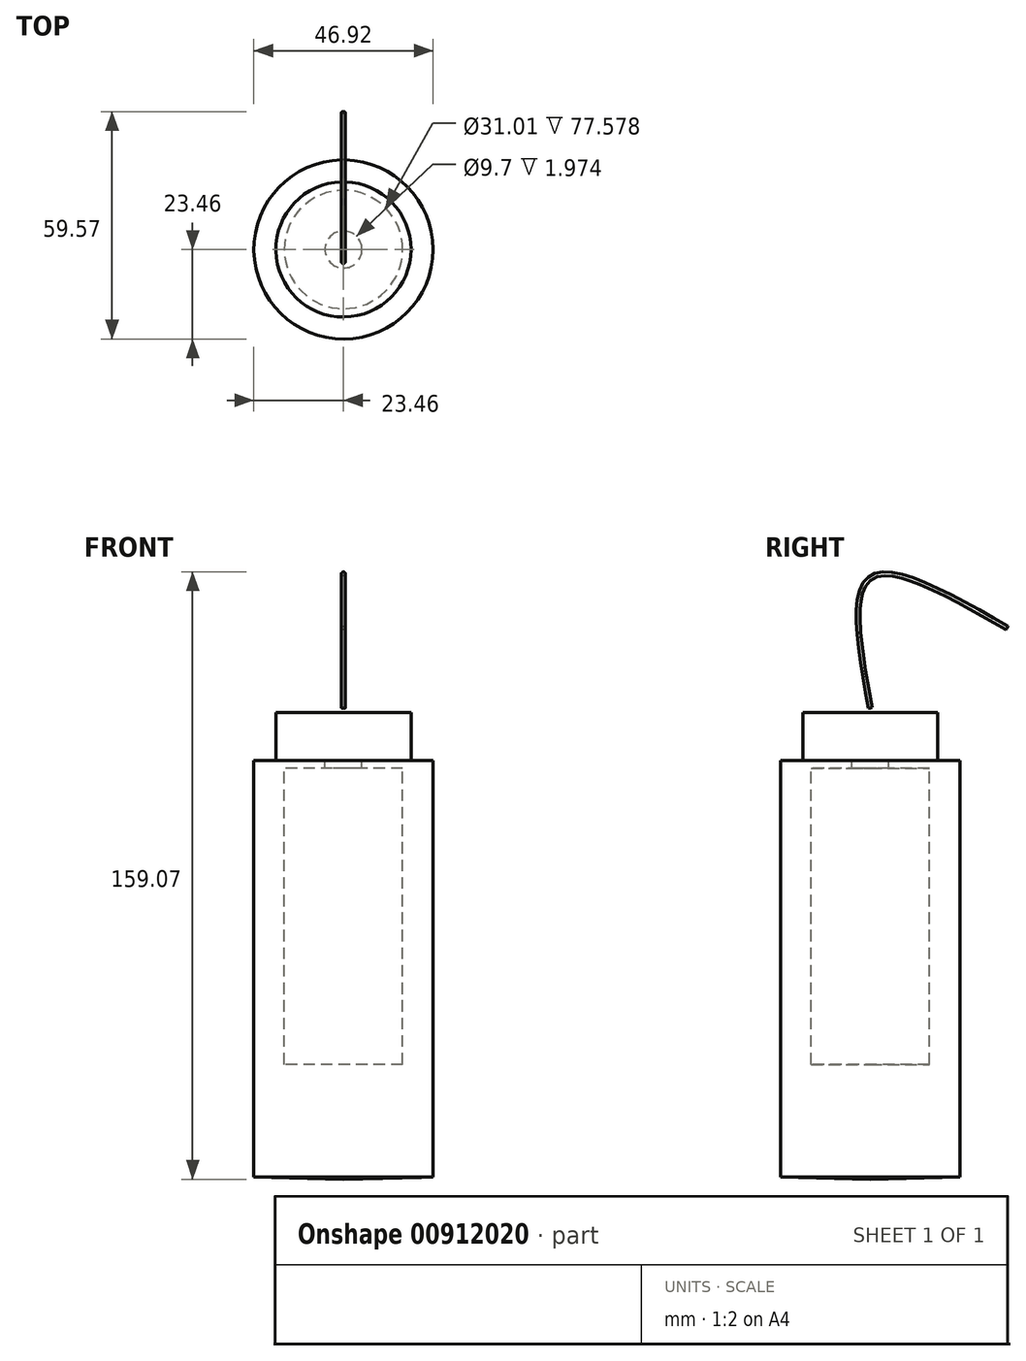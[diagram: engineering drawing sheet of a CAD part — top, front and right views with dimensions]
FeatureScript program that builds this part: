
annotation { "Feature Type Name" : "Feature", "Feature Type Description" : "" }
export const myFeature = defineFeature(function(context is Context, id is Id, definition is map)
    precondition{}
    {
        {
            var Q0;
            Q0=qCreatedBy(makeId("Front.planeOp"),FACE);
            var sketch = newSketch(context, id + "F0", { "sketchPlane" : qUnion([Q0])});
            skLineSegment(sketch, "E0", {"start": v(0, -24.73) * mm, "end": v(0, -54.83) * mm});
            skLineSegment(sketch, "E1", {"start": v(0, 54.83) * mm, "end": v(4.85, 54.83) * mm});
            skLineSegment(sketch, "E2", {"start": v(23.46, 54.83) * mm, "end": v(23.46, -54.25) * mm});
            skLineSegment(sketch, "E3", {"start": v(23.46, -54.25) * mm, "end": v(0, -54.83) * mm});
            skLineSegment(sketch, "E4", {"start": v(17.7, 54.83) * mm, "end": v(17.7, 67.48) * mm});
            skLineSegment(sketch, "E5", {"start": v(8.85, 67.48) * mm, "end": v(0, 67.48) * mm});
            skLineSegment(sketch, "E6", {"start": v(122.75, 33.82) * mm, "end": v(122.75, 27.49) * mm});
            skLineSegment(sketch, "E7", {"start": v(0, 67.48) * mm, "end": v(0, 54.83) * mm});
            skLineSegment(sketch, "E8", {"start": v(15.5, 52.85) * mm, "end": v(15.5, -24.73) * mm});
            skLineSegment(sketch, "E9", {"start": v(15.5, -24.73) * mm, "end": v(0, -24.73) * mm});
            skLineSegment(sketch, "E10", {"start": v(15.5, 52.85) * mm, "end": v(4.85, 52.85) * mm});
            skLineSegment(sketch, "E11", {"start": v(4.85, 52.85) * mm, "end": v(4.85, 54.83) * mm});
            skLineSegment(sketch, "E12.trimOffspring", {"start": v(17.7, 54.83) * mm, "end": v(23.46, 54.83) * mm});
            skLineSegment(sketch, "E13", {"start": v(8.85, 67.48) * mm, "end": v(17.7, 67.48) * mm});
            skSolve(sketch);
        }
        {
            var Q0;
            Q0=makeQuery(id+"F0.imprint","IMPRINT",FACE,{"disambiguationData":[TD([[makeQuery(id+"F0.imprint","IMPRINT",EDGE,{"derivedFrom":sQuery(id+"F0.wireOp",EDGE,"ec97caab-534c-41fb-974d-b1bae08ad47f")}),-1.0]])]});
            var Q1;
            Q1=makeQuery(id+"F0.imprint","IMPRINT",FACE,{"disambiguationData":[TD([[makeQuery(id+"F0.imprint","IMPRINT",EDGE,{"derivedFrom":sQuery(id+"F0.wireOp",EDGE,"E0")}),1.0]])]});
            var Q2;
            Q2=sQuery(id+"F0.wireOp",EDGE,"E7");
            revolve(context, id + "F1", {"surfaceOperationType" : NewSurfaceOperationType.NEW, "entities" : qUnion([Q0, Q1]), "axis" : qUnion([Q2]), "revolveType" : RevolveType.FULL});
        }
        {
            var Q0;
            Q0=qCreatedBy(makeId("Right.planeOp"),FACE);
            var sketch = newSketch(context, id + "F2", { "sketchPlane" : qUnion([Q0])});
            skFitSpline(sketch, "E14", {"points": [v(0, 68.6) * mm, v(0, 102.7) * mm, v(35.86, 89.59) * mm], "startDerivative": vector(-16.94, 93.4) * mm, "endDerivative": vector(87.67, -50.09) * mm});
            skSolve(sketch);
        }
        {
            var Q0;
            Q0=sQuery(id+"F2.wireOp",VERTEX,"E14.end");
            var Q1;
            Q1=sQuery(id+"F2.wireOp",EDGE,"E14");
            cPlane(context, id + "F3", {"entities" : qUnion([Q0, Q1]), "cplaneType" : CPlaneType.CURVE_POINT, "offset" : 25.4 * mm, "width" : 152.4 * mm, "height" : 152.4 * mm});
        }
        {
            var Q0;
            Q0=qCreatedBy(id+"F3.planeOp",FACE);
            var sketch = newSketch(context, id + "F4", { "sketchPlane" : qUnion([Q0])});
            skCircle(sketch, "E15", {"center": v(0, 95.57) * mm, "radius": 0.5 * mm});
            skSolve(sketch);
        }
        {
            var Q0;
            Q0=makeQuery(id+"F4.imprint","IMPRINT",FACE,{"disambiguationData":[TD([[makeQuery(id+"F4.imprint","IMPRINT",EDGE,{"derivedFrom":sQuery(id+"F4.wireOp",EDGE,"E15")}),1.0]])]});
            var Q1;
            Q1=sQuery(id+"F2.wireOp",EDGE,"E14");
            sweep(context, id + "F5", {"profiles" : qUnion([Q0]), "path" : qUnion([Q1])});
        }
    });
